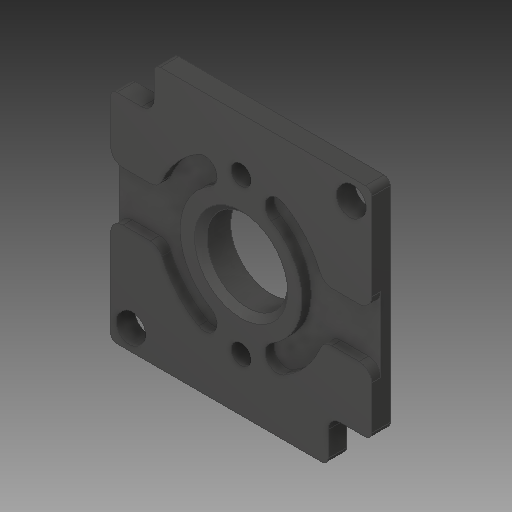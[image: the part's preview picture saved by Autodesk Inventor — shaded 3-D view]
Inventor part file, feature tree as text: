
AUTODESK INVENTOR PART (.ipt)
format: ipt  version: 2017 (Build 210142000, 142)  size: 290,304 bytes
history: native  units: in
note: dims shown in document units (in); Inventor stores cm internally (conversion verified against a paired STEP export)
features: fillet x1
ambient origin geometry x8: Origin, YZ Plane, XZ Plane, XY Plane, X Axis, Y Axis, Z Axis, Center Point
bodies: Solid1 (feature_tree)
feature tree (1):
  fillet  "Fillet4"  [1 undecoded]
note: 1 required parameter value undecoded (feature->parameter linkage not recoverable at this tier; creation-order binding heuristic only, values carry confidence <= 0.55)
